# Revit family: НЕВАТОМ_Дверь вентиляционная_20220407
name_source: partatom
category: Арматура воздуховодов
revit_build: Autodesk Revit 2017 (Build: 20170118_1100(x64)
units: mm (PartAtom-declared; Revit-internal decimal feet)

## family parameters
Всегда вертикально = Да
Заголовок OmniClass = Doors
Номер OmniClass = 23.30.10.00
Общий = Нет
Основа = Стена
При загрузке вырезать с полостями = Нет
Размер круглого соединителя = Использовать диаметр
Тип детали = Присоединяется

## types (2) — shared parameters
ADSK_Единица измерения = шт
ADSK_Завод-изготовитель = NEVATOM
ADSK_Масса_Текст = кг
ADSK_Материал наименование = Оцинкованная сталь
ADSK_Размер_Ширина = 45 мм
H коробки = 40 мм
Nevatom_URL = https://t.me
Зазор = 5 мм
Замыкание стены = По основе
Левое = Да
Материал каркаса = Материал каркаса
Правое = Нет
Толщина каркаса = 45 мм
zero-valued in all types: ADSK_Масса

## per-type parameters (varying)
| type | A | ADSK_Марка | ADSK_Наименование | ADSK_Размер_Высота | ADSK_Размер_Длина | B |
| 900*400 | 985 мм | 900х400 | ДВЕРЬ ВЕНТИЛЯЦИОННАЯ | 985 мм | 490 мм | 490 мм |
| 1250*500 | 1335 мм | 1250х500 |  | 1335 мм | 590 мм | 590 мм |
